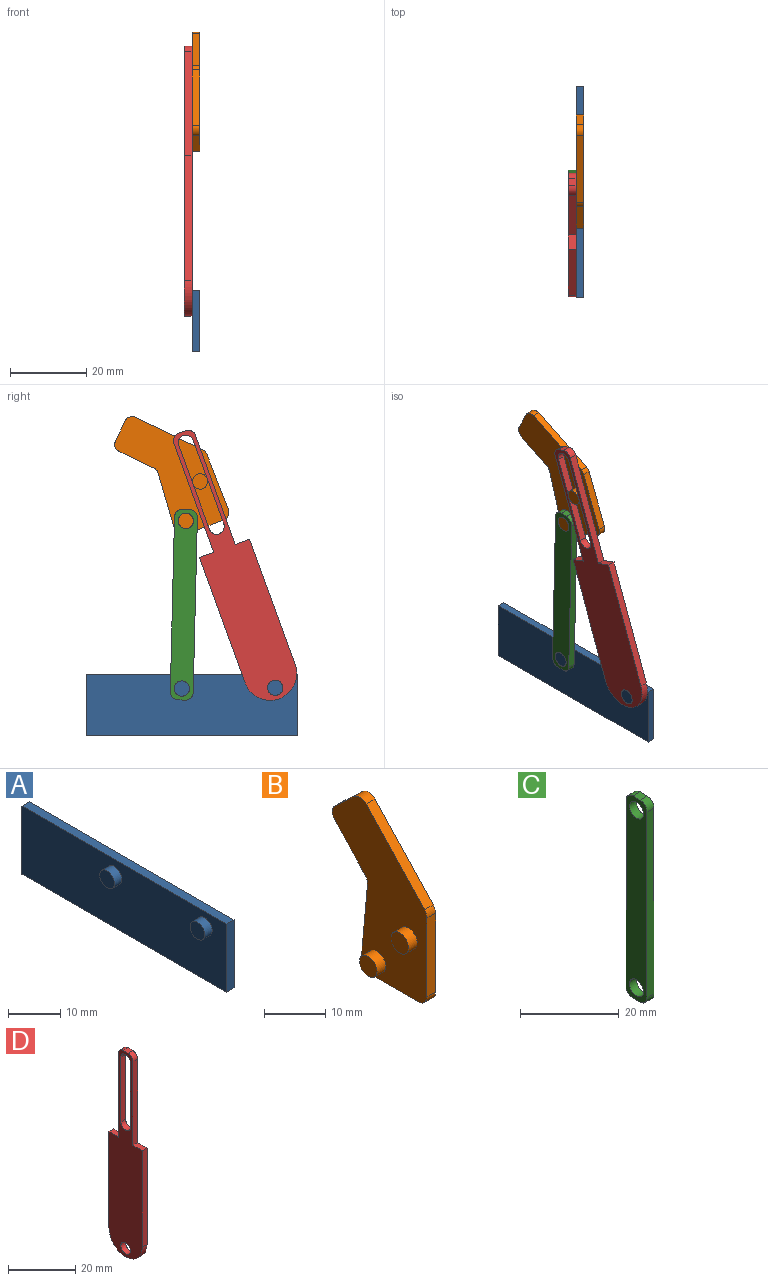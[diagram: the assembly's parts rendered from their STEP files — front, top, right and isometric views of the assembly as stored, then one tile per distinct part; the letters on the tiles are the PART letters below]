
ASSEMBLY  parts=4 mates=4
PART A: 10 faces, bbox 4x55.6x16 mm
  f0: plane 55.57x2mm, normal (0,0,-1), area 111.1mm2, adj f1,f3,f4,f5
  f1: plane 16.02x2mm, normal (0,1,0), area 32mm2, adj f0,f2,f4,f5
  f2: plane 55.57x2mm, normal (0,0,1), area 111.1mm2, adj f1,f3,f4,f5
  f3: plane 16.02x2mm, normal (0,-1,0), area 32mm2, adj f0,f2,f4,f5
  f4: plane 55.57x16.02mm, normal (1,0,0), area 890mm2, adj f0,f1,f2,f3
  f5: plane 55.57x16.02mm, normal (-1,0,0), area 864.8mm2, adj f0,f1,f2,f3,f6,f8
  f6: cylinder r=2mm len=4mm, axis (1,0,0), area 25.1mm2, adj f5,f7
  f7: plane 4x4mm, normal (-1,0,0), area 12.6mm2, adj f6
  f8: cylinder r=2mm len=4mm, axis (1,0,0), area 25.1mm2, adj f5,f9
  f9: plane 4x4mm, normal (-1,0,0), area 12.6mm2, adj f8
PART B: 18 faces, bbox 4x21.7x34.1 mm
  f0: plane 7.52x6.99mm, normal (0,0.73,-0.68), area 20.5mm2, adj f1,f11,f12,f13
  f1: cylinder r=2mm len=2.83mm, axis (-1,0,0), area 6.3mm2, adj f0,f2,f12,f13
  f2: plane 4.37x4.06mm, normal (0,0.68,0.73), area 11.9mm2, adj f1,f3,f12,f13
  f3: cylinder r=2mm len=2.83mm, axis (-1,0,0), area 6.3mm2, adj f2,f4,f12,f13
  f4: plane 14.39x13.37mm, normal (0,-0.73,0.68), area 39.3mm2, adj f3,f5,f12,f13
  f5: cylinder r=2mm len=2mm, axis (-1,0,0), area 3mm2, adj f4,f6,f12,f13
  f6: plane 15.72x2mm, normal (0,-1,0), area 31.4mm2, adj f5,f7,f12,f13
  f7: cylinder r=2mm len=2mm, axis (-1,0,0), area 6.3mm2, adj f6,f8,f12,f13
  f8: plane 11.08x2mm, normal (0,0,-1), area 22.2mm2, adj f7,f9,f12,f13
  f9: cylinder r=2mm len=2.18mm, axis (-1,0,0), area 6.6mm2, adj f8,f10,f12,f13
  f10: plane 15.44x2mm, normal (0,1,0.09), area 31mm2, adj f9,f11,f12,f13
  f11: cylinder r=2mm len=2mm, axis (-1,0,0), area 3.4mm2, adj f0,f10,f12,f13
  f12: plane 34.11x21.74mm, normal (1,0,0), area 441mm2, adj f0,f1,f2,f3,f4,f5,f6,f7
  f13: plane 34.11x21.74mm, normal (-1,0,0), area 415.9mm2, adj f0,f1,f2,f3,f4,f5,f6,f7
  f14: cylinder r=2mm len=4mm, axis (1,0,0), area 25.1mm2, adj f13,f15
  f15: plane 4x4mm, normal (-1,0,0), area 12.6mm2, adj f14
  f16: cylinder r=2mm len=4mm, axis (1,0,0), area 25.1mm2, adj f13,f17
  f17: plane 4x4mm, normal (-1,0,0), area 12.6mm2, adj f16
PART C: 12 faces, bbox 2x6x50 mm
  f0: plane 46x2mm, normal (0,1,0), area 92mm2, adj f1,f9,f10,f11
  f1: cylinder r=2mm len=2mm, axis (-1,0,0), area 6.3mm2, adj f0,f2,f10,f11
  f2: plane 2x2mm, normal (0,0,1), area 4mm2, adj f1,f3,f10,f11
  f3: cylinder r=2mm len=2mm, axis (-1,0,0), area 6.3mm2, adj f2,f4,f10,f11
  f4: plane 46x2mm, normal (0,-1,0), area 92mm2, adj f3,f5,f10,f11
  f5: cylinder r=2mm len=2mm, axis (-1,0,0), area 6.3mm2, adj f4,f6,f10,f11
  f6: plane 2x2mm, normal (0,0,-1), area 4mm2, adj f5,f9,f10,f11
  f7: cylinder r=2mm len=4mm, axis (-1,0,0), area 25.1mm2, adj f10,f11
  f8: cylinder r=2mm len=4mm, axis (-1,0,0), area 25.1mm2, adj f10,f11
  f9: cylinder r=2mm len=2mm, axis (-1,0,0), area 6.3mm2, adj f0,f6,f10,f11
  f10: plane 50x6mm, normal (1,0,0), area 271.4mm2, adj f0,f1,f2,f3,f4,f5,f6,f7
  f11: plane 50x6mm, normal (-1,0,0), area 271.4mm2, adj f0,f1,f2,f3,f4,f5,f6,f7
PART D: 17 faces, bbox 2x14x74.5 mm
  f0: cylinder r=2mm len=4mm, axis (-1,0,0), area 12.6mm2, adj f1,f14,f15,f16
  f1: plane 23.43x2mm, normal (0,-1,0), area 46.9mm2, adj f0,f2,f15,f16
  f2: cylinder r=2mm len=4mm, axis (-1,0,0), area 12.6mm2, adj f1,f14,f15,f16
  f3: plane 4x2mm, normal (0,0,1), area 8mm2, adj f4,f13,f15,f16
  f4: plane 30.5x2mm, normal (0,1,0), area 61mm2, adj f3,f5,f15,f16
  f5: cylinder r=2mm len=2mm, axis (-1,0,0), area 6.3mm2, adj f4,f6,f15,f16
  f6: plane 2x2mm, normal (0,0,1), area 4mm2, adj f5,f7,f15,f16
  f7: cylinder r=2mm len=2mm, axis (-1,0,0), area 6.3mm2, adj f6,f8,f15,f16
  f8: plane 30.5x2mm, normal (0,-1,0), area 61mm2, adj f7,f9,f15,f16
  f9: plane 4x2mm, normal (0,0,1), area 8mm2, adj f8,f10,f15,f16
  f10: plane 35x2mm, normal (0,-1,0), area 70mm2, adj f9,f11,f15,f16
  f11: cylinder r=7mm len=14mm, axis (-1,0,0), area 44mm2, adj f10,f13,f15,f16
  f12: cylinder r=2mm len=4mm, axis (-1,0,0), area 25.1mm2, adj f15,f16
  f13: plane 35x2mm, normal (0,1,0), area 70mm2, adj f3,f11,f15,f16
  f14: plane 23.43x2mm, normal (0,1,0), area 46.9mm2, adj f0,f2,f15,f16
  f15: plane 74.5x14mm, normal (1,0,0), area 641.4mm2, adj f0,f1,f2,f3,f4,f5,f6,f7
  f16: plane 74.5x14mm, normal (-1,0,0), area 641.4mm2, adj f0,f1,f2,f3,f4,f5,f6,f7
PLACE A at identity fixed
PLACE B rot(axis=(-1,0,0),21.3deg) t=(0,-7.21,-21.53)mm
PLACE C rot(axis=(1,0,0),1.4deg) t=(-2,61.96,-20.78)mm
PLACE D rot(axis=(-1,0,0),20deg) t=(-2,5.3,-14.09)mm
MATE pin_slot B.f16 <-> D.f16  axis (-1,0,0) through (-2,13.29,24.39)mm
MATE revolute B.f14 <-> C.f7  axis (-1,0,0) through (-2,17.04,14.03)mm
MATE revolute C.f8 <-> A.f6  axis (-1,0,0) through (-2,18.09,-29.95)mm
MATE revolute D.f12 <-> A.f8  axis (-1,0,0) through (-2,-6.42,-29.76)mm
